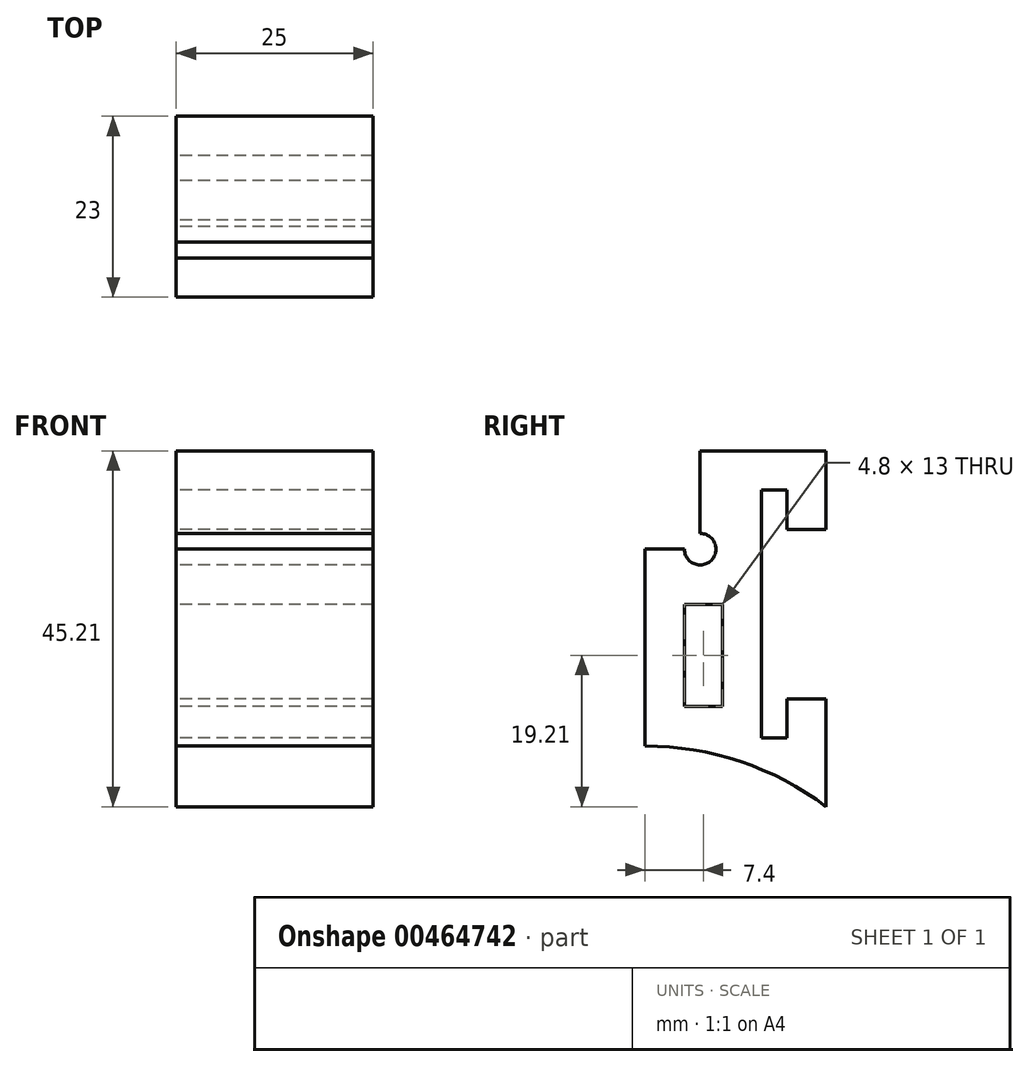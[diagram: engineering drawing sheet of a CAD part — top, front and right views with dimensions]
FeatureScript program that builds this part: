
annotation { "Feature Type Name" : "Feature", "Feature Type Description" : "" }
export const myFeature = defineFeature(function(context is Context, id is Id, definition is map)
    precondition{}
    {
        {
            var Q0;
            Q0=qCreatedBy(makeId("Right.planeOp"),FACE);
            var sketch = newSketch(context, id + "F0", { "sketchPlane" : qUnion([Q0])});
            skCircle(sketch, "E0", {"center": v(0, 0) * mm, "radius": 38.15 * mm});
            skLineSegment(sketch, "E1", {"start": v(0, 0) * mm, "end": v(0, 38.15) * mm});
            skLineSegment(sketch, "E2", {"start": v(0, 38.15) * mm, "end": v(0, 38.15) * mm});
            skLineSegment(sketch, "E3", {"start": v(0, 63.15) * mm, "end": v(0, 38.15) * mm});
            skLineSegment(sketch, "E4", {"start": v(0, 63.15) * mm, "end": v(7, 63.15) * mm});
            skLineSegment(sketch, "E5", {"start": v(7, 63.15) * mm, "end": v(7, 75.65) * mm});
            skLineSegment(sketch, "E6", {"start": v(7, 75.65) * mm, "end": v(23, 75.65) * mm});
            skLineSegment(sketch, "E7", {"start": v(23, 75.65) * mm, "end": v(23, 30.44) * mm});
            skCircle(sketch, "E8", {"center": v(7, 63.15) * mm, "radius": 2 * mm});
            skLineSegment(sketch, "E9.bottom", {"start": v(14.8, 70.65) * mm, "end": v(18, 70.65) * mm});
            skLineSegment(sketch, "E9.top", {"start": v(14.8, 39.15) * mm, "end": v(18, 39.15) * mm});
            skLineSegment(sketch, "E9.left", {"start": v(14.8, 70.65) * mm, "end": v(14.8, 39.15) * mm});
            skLineSegment(sketch, "E9.right", {"start": v(18, 70.65) * mm, "end": v(18, 39.15) * mm});
            skLineSegment(sketch, "E10", {"start": v(0, 50.65) * mm, "end": v(14.8, 50.65) * mm, "construction": true});
            skLineSegment(sketch, "E11.bottom", {"start": v(18, 65.65) * mm, "end": v(23, 65.65) * mm});
            skLineSegment(sketch, "E11.top", {"start": v(18, 44.15) * mm, "end": v(23, 44.15) * mm});
            skLineSegment(sketch, "E11.left", {"start": v(18, 65.65) * mm, "end": v(18, 44.15) * mm});
            skLineSegment(sketch, "E11.right", {"start": v(23, 65.65) * mm, "end": v(23, 44.15) * mm});
            skLineSegment(sketch, "E12", {"start": v(18, 39.15) * mm, "end": v(18, 33.64) * mm});
            skLineSegment(sketch, "E13.bottom", {"start": v(5, 56.15) * mm, "end": v(9.8, 56.15) * mm});
            skLineSegment(sketch, "E13.top", {"start": v(5, 43.15) * mm, "end": v(9.8, 43.15) * mm});
            skLineSegment(sketch, "E13.left", {"start": v(5, 56.15) * mm, "end": v(5, 43.15) * mm});
            skLineSegment(sketch, "E13.right", {"start": v(9.8, 56.15) * mm, "end": v(9.8, 43.15) * mm});
            skSolve(sketch);
        }
        {
            var Q0;
            {var subQ9=sQuery(id+"F0.wireOp",EDGE,"E3");Q0=makeQuery(id+"F0.imprint","IMPRINT",FACE,{"disambiguationData":[TD([[makeQuery(id+"F0.imprint","IMPRINT",EDGE,{"derivedFrom":subQ9}),1.0]])]});}
            var Q1;
            {var subQ0=sQuery(id+"F0.wireOp",EDGE,"E11.top");Q1=makeQuery(id+"F0.imprint","IMPRINT",FACE,{"disambiguationData":[TD([[makeQuery(id+"F0.imprint","IMPRINT",EDGE,{"derivedFrom":subQ0}),-1.0]])]});}
            extrude(context, id + "F1", {"entities" : qUnion([Q0, Q1]), "depth" : 25 * mm});
        }
    });
